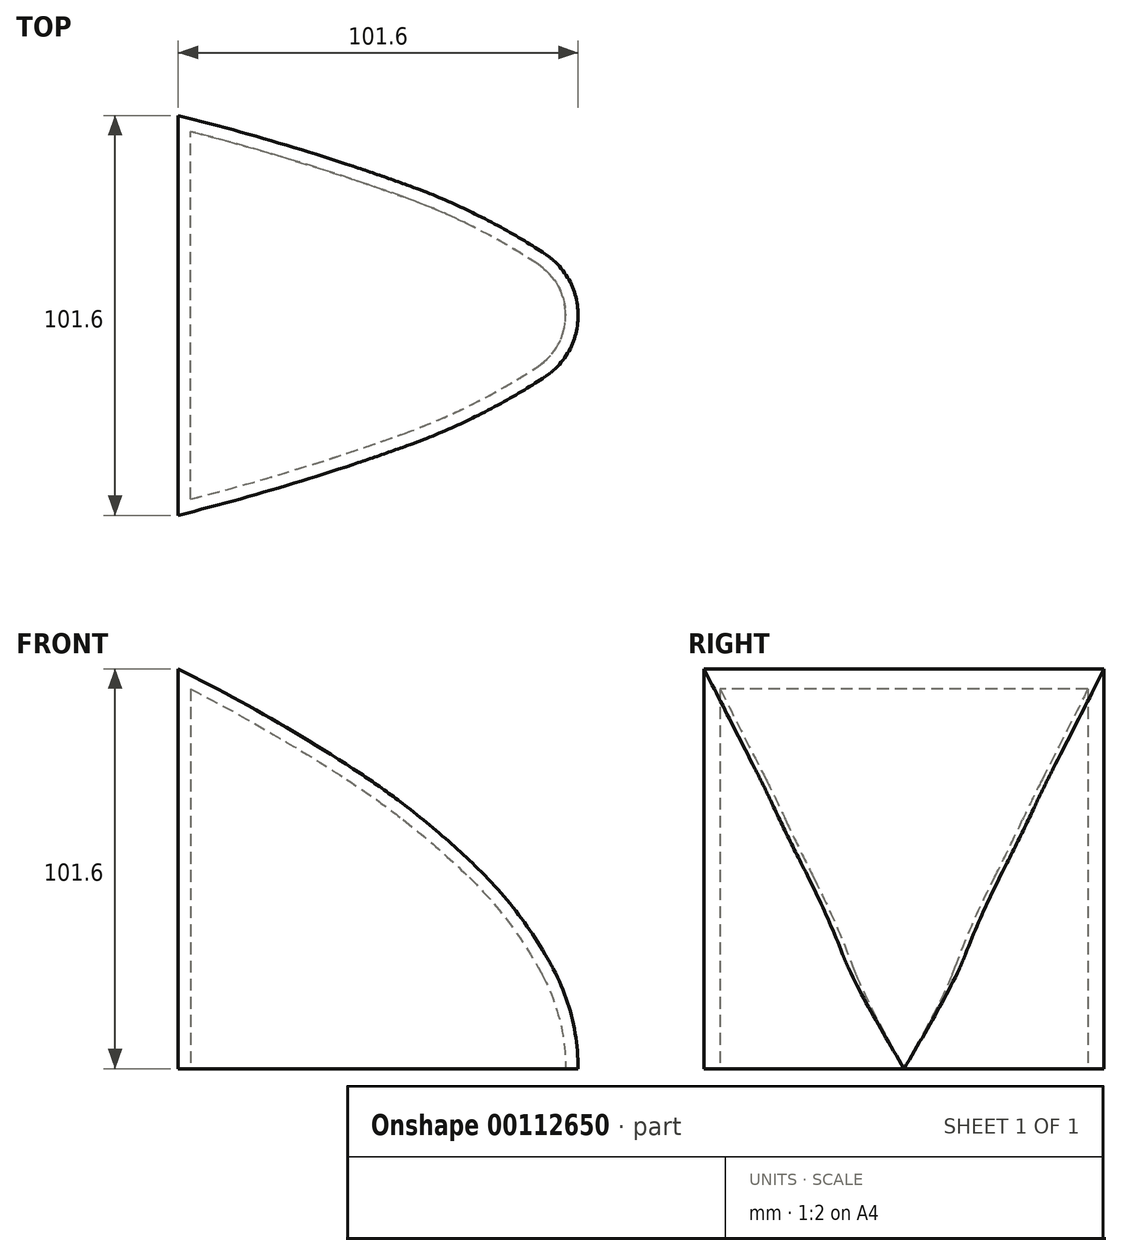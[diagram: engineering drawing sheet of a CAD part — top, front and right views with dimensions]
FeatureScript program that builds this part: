
annotation { "Feature Type Name" : "Feature", "Feature Type Description" : "" }
export const myFeature = defineFeature(function(context is Context, id is Id, definition is map)
    precondition{}
    {
        {
            var Q0;
            Q0=qCreatedBy(makeId("Top.planeOp"),FACE);
            var sketch = newSketch(context, id + "F0", { "sketchPlane" : qUnion([Q0])});
            skLineSegment(sketch, "E0", {"start": v(0, 0) * mm, "end": v(-25.4, 0) * mm, "construction": true});
            skLineSegment(sketch, "E1", {"start": v(0, 0) * mm, "end": v(0, -25.4) * mm, "construction": true});
            skLineSegment(sketch, "E2", {"start": v(0, -25.4) * mm, "end": v(-25.4, -25.4) * mm, "construction": true});
            skLineSegment(sketch, "E3", {"start": v(-25.4, 0) * mm, "end": v(-25.4, -25.4) * mm, "construction": true});
            skArc(sketch, "E4", {"start": v(-8.41, -15.61) * mm, "mid": v(-2.24, -8.87) * mm, "end": v(0, 0) * mm});
            skLineSegment(sketch, "E5", {"start": v(0, 0) * mm, "end": v(-25.4, -25.4) * mm, "construction": true});
            skLineSegment(sketch, "E6", {"start": v(-25.4, -25.4) * mm, "end": v(-50.8, -25.4) * mm, "construction": true});
            skLineSegment(sketch, "E7", {"start": v(-50.8, -25.4) * mm, "end": v(-76.2, -25.4) * mm, "construction": true});
            skLineSegment(sketch, "E8", {"start": v(-76.2, -25.4) * mm, "end": v(-76.2, -50.8) * mm, "construction": true});
            skLineSegment(sketch, "E9", {"start": v(-25.4, -25.4) * mm, "end": v(-76.2, -50.8) * mm, "construction": true});
            skLineSegment(sketch, "E10", {"start": v(0, -25.4) * mm, "end": v(0, -50.8) * mm, "construction": true});
            skLineSegment(sketch, "E11", {"start": v(0, -50.8) * mm, "end": v(-25.4, -50.8) * mm, "construction": true});
            skLineSegment(sketch, "E12", {"start": v(-25.4, -25.4) * mm, "end": v(-25.4, -50.8) * mm, "construction": true});
            skLineSegment(sketch, "E13", {"start": v(-76.2, -25.4) * mm, "end": v(-101.6, -25.4) * mm, "construction": true});
            skLineSegment(sketch, "E14", {"start": v(-101.6, -25.4) * mm, "end": v(-101.6, -50.8) * mm, "construction": true});
            skLineSegment(sketch, "E15", {"start": v(-76.2, -50.8) * mm, "end": v(-50.8, -50.8) * mm, "construction": true});
            skLineSegment(sketch, "E16", {"start": v(-50.8, -50.8) * mm, "end": v(-25.4, -50.8) * mm, "construction": true});
            skLineSegment(sketch, "E17", {"start": v(-76.2, -50.8) * mm, "end": v(-101.6, -50.8) * mm, "construction": true});
            skLineSegment(sketch, "E18", {"start": v(-101.6, -50.8) * mm, "end": v(-127, -50.8) * mm, "construction": true});
            skLineSegment(sketch, "E19", {"start": v(-127, -50.8) * mm, "end": v(-152.4, -50.8) * mm, "construction": true});
            skLineSegment(sketch, "E20", {"start": v(-152.4, -50.8) * mm, "end": v(-177.8, -50.8) * mm, "construction": true});
            skLineSegment(sketch, "E21", {"start": v(-177.8, -50.8) * mm, "end": v(-203.2, -50.8) * mm, "construction": true});
            skLineSegment(sketch, "E22", {"start": v(-203.2, -50.8) * mm, "end": v(-203.2, -76.2) * mm, "construction": true});
            skLineSegment(sketch, "E23", {"start": v(-101.6, -50.8) * mm, "end": v(-203.2, -76.2) * mm, "construction": true});
            skArc(sketch, "E24", {"start": v(-101.6, -50.8) * mm, "mid": v(-72.29, -42.69) * mm, "end": v(-43.42, -33.11) * mm});
            skArc(sketch, "E25", {"start": v(-43.42, -33.11) * mm, "mid": v(-25.4, -25.4) * mm, "end": v(-8.41, -15.61) * mm});
            skLineSegment(sketch, "E26", {"start": v(0, 0) * mm, "end": v(-101.6, 0) * mm});
            skLineSegment(sketch, "E27", {"start": v(-101.6, -50.8) * mm, "end": v(-101.6, 0) * mm});
            skArc(sketch, "E28", {"start": v(0, 0) * mm, "mid": v(-2.24, 8.87) * mm, "end": v(-8.41, 15.61) * mm});
            skArc(sketch, "E29", {"start": v(-8.41, 15.61) * mm, "mid": v(-25.4, 25.4) * mm, "end": v(-43.42, 33.11) * mm});
            skLineSegment(sketch, "E30", {"start": v(-25.4, 0) * mm, "end": v(-25.4, 25.4) * mm, "construction": true});
            skArc(sketch, "E31", {"start": v(-43.42, 33.11) * mm, "mid": v(-72.29, 42.69) * mm, "end": v(-101.6, 50.8) * mm});
            skLineSegment(sketch, "E32", {"start": v(-101.6, 0) * mm, "end": v(-101.6, 50.8) * mm});
            skSolve(sketch);
        }
        {
            var Q0;
            Q0=makeQuery(id+"F0.imprint","IMPRINT",FACE,{"disambiguationData":[TD([[makeQuery(id+"F0.imprint","IMPRINT",EDGE,{"derivedFrom":sQuery(id+"F0.wireOp",EDGE,"E4")}),1.0]])]});
            var Q1;
            Q1=makeQuery(id+"F0.imprint","IMPRINT",FACE,{"disambiguationData":[TD([[makeQuery(id+"F0.imprint","IMPRINT",EDGE,{"derivedFrom":sQuery(id+"F0.wireOp",EDGE,"E26")}),-1.0]])]});
            extrude(context, id + "F1", {"entities" : qUnion([Q0, Q1]), "depth" : 203.2 * mm});
        }
        {
            var Q0;
            Q0=qCreatedBy(makeId("Front.planeOp"),FACE);
            cPlane(context, id + "F2", {"entities" : qUnion([Q0]), "cplaneType" : CPlaneType.OFFSET, "offset" : 50.8 * mm, "width" : 152.4 * mm, "height" : 152.4 * mm});
        }
        {
            var Q0;
            Q0=qCreatedBy(id+"F2.planeOp",FACE);
            var sketch = newSketch(context, id + "F3", { "sketchPlane" : qUnion([Q0])});
            skLineSegment(sketch, "E33", {"start": v(-101.6, 0) * mm, "end": v(-101.6, 101.6) * mm});
            skLineSegment(sketch, "E34.top", {"start": v(-101.6, 203.2) * mm, "end": v(0, 203.2) * mm});
            skLineSegment(sketch, "E34.left", {"start": v(-101.6, 101.6) * mm, "end": v(-101.6, 203.2) * mm});
            skLineSegment(sketch, "E34.right", {"start": v(0, 0) * mm, "end": v(0, 203.2) * mm});
            skArc(sketch, "E35", {"start": v(0, 0) * mm, "mid": v(-1.61, 13.1) * mm, "end": v(-6.35, 25.4) * mm});
            skLineSegment(sketch, "E36", {"start": v(-6.35, 25.4) * mm, "end": v(0, 25.4) * mm, "construction": true});
            skArc(sketch, "E37", {"start": v(-57.15, 76.2) * mm, "mid": v(-79.02, 89.53) * mm, "end": v(-101.6, 101.6) * mm});
            skLineSegment(sketch, "E38", {"start": v(0, 50.8) * mm, "end": v(-25.4, 50.8) * mm, "construction": true});
            skArc(sketch, "E39", {"start": v(-6.35, 25.4) * mm, "mid": v(-14.9, 38.83) * mm, "end": v(-25.4, 50.8) * mm});
            skLineSegment(sketch, "E40", {"start": v(0, 76.2) * mm, "end": v(-57.15, 76.2) * mm, "construction": true});
            skArc(sketch, "E41", {"start": v(-25.4, 50.8) * mm, "mid": v(-40.65, 64.29) * mm, "end": v(-57.15, 76.2) * mm});
            skSolve(sketch);
        }
        {
            var Q0;
            Q0 = qSketchRegion(id + "F3", true);
            var Q1;
            Q1=makeQuery(id+"F1.opExtrude","SWEPT_FACE",FACE,{"disambiguationData":[OSD([sQuery(id+"F0.wireOp",EDGE,"E31")])]});
            extrude(context, id + "F4", {"entities" : qUnion([Q0]), "operationType" : NewBodyOperationType.REMOVE, "endBound" : BoundingType.UP_TO_SURFACE, "oppositeDirection" : true, "endBoundEntityFace" : qUnion([Q1]), "depth" : 25.4 * mm});
        }
        {
            var Q0;
            Q0=makeQuery(id+"F1.opExtrude","CAP_FACE",FACE,{"disambiguationData":[OSD([sQuery(id+"F0.wireOp",EDGE,"E4"),sQuery(id+"F0.wireOp",EDGE,"E24"),sQuery(id+"F0.wireOp",EDGE,"E25"),sQuery(id+"F0.wireOp",EDGE,"E27"),sQuery(id+"F0.wireOp",EDGE,"E28"),sQuery(id+"F0.wireOp",EDGE,"E29"),sQuery(id+"F0.wireOp",EDGE,"E31"),sQuery(id+"F0.wireOp",EDGE,"E32")])],"isStart":true});
            shell(context, id + "F5", {"entities" : qUnion([Q0]), "thickness" : 3.17 * mm});
        }
    });
